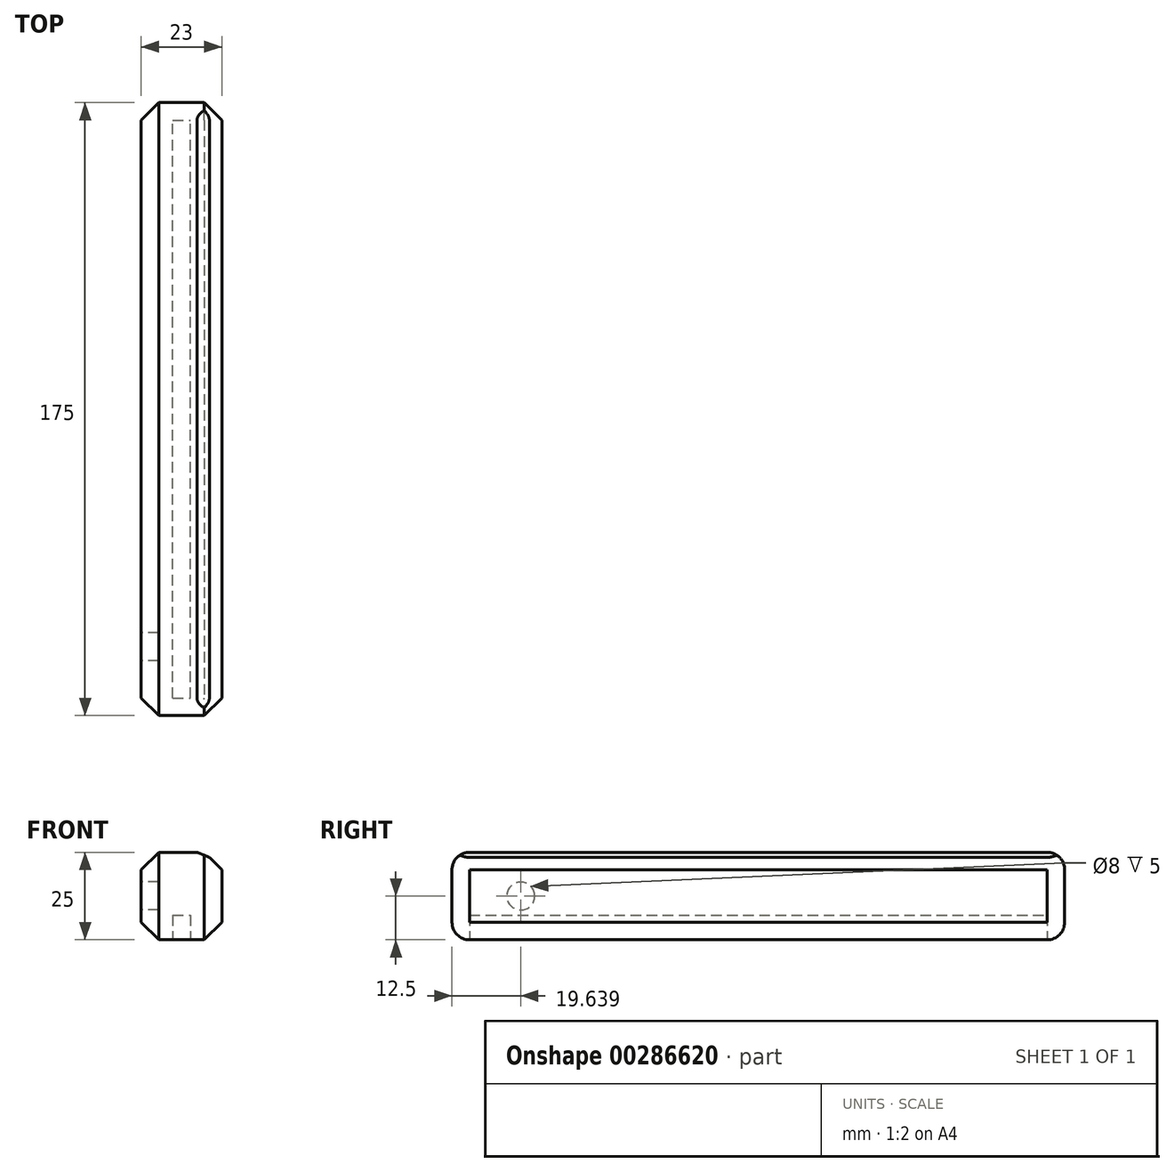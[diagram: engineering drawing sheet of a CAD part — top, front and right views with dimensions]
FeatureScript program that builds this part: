
annotation { "Feature Type Name" : "Feature", "Feature Type Description" : "" }
export const myFeature = defineFeature(function(context is Context, id is Id, definition is map)
    precondition{}
    {
        {
            var Q0;
            Q0=qCreatedBy(makeId("Front.planeOp"),FACE);
            var sketch = newSketch(context, id + "F0", { "sketchPlane" : qUnion([Q0])});
            skLineSegment(sketch, "E0.bottom", {"start": v(-11.5, 12.5) * mm, "end": v(11.5, 12.5) * mm});
            skLineSegment(sketch, "E0.top", {"start": v(-11.5, -12.5) * mm, "end": v(11.5, -12.5) * mm});
            skLineSegment(sketch, "E0.left", {"start": v(-11.5, 12.5) * mm, "end": v(-11.5, -12.5) * mm});
            skLineSegment(sketch, "E0.right", {"start": v(11.5, 12.5) * mm, "end": v(11.5, -12.5) * mm});
            skPoint(sketch, "E0.middle", {"position": v(0, 0) * mm});
            skSolve(sketch);
        }
        {
            var Q0;
            Q0=makeQuery(id+"F0.imprint","IMPRINT",FACE,{"disambiguationData":[TD([[makeQuery(id+"F0.imprint","IMPRINT",EDGE,{"derivedFrom":sQuery(id+"F0.wireOp",EDGE,"E0.bottom")}),-1.0]])]});
            extrude(context, id + "F1", {"entities" : qUnion([Q0]), "depth" : 175 * mm});
        }
        {
            var Q0;
            Q0=makeQuery(id+"F1.opExtrude","CAP_EDGE",EDGE,{"disambiguationData":[OSD([sQuery(id+"F0.wireOp",EDGE,"E0.bottom")])],"isStart":false});
            var Q1;
            Q1=makeQuery(id+"F1.opExtrude","CAP_EDGE",EDGE,{"disambiguationData":[OSD([sQuery(id+"F0.wireOp",EDGE,"E0.top")])],"isStart":false});
            var Q2;
            Q2=makeQuery(id+"F1.opExtrude","CAP_EDGE",EDGE,{"disambiguationData":[OSD([sQuery(id+"F0.wireOp",EDGE,"E0.bottom")])],"isStart":true});
            var Q3;
            Q3=makeQuery(id+"F1.opExtrude","CAP_EDGE",EDGE,{"disambiguationData":[OSD([sQuery(id+"F0.wireOp",EDGE,"E0.top")])],"isStart":true});
            fillet(context, id + "F2", {"entities" : qUnion([Q0, Q1, Q2, Q3]), "radius" : 5 * mm, "tangentPropagation" : true, "allowEdgeOverflow" : false});
        }
        {
            var Q0;
            Q0=makeQuery(id+"F1.opExtrude","SWEPT_FACE",FACE,{"disambiguationData":[OSD([sQuery(id+"F0.wireOp",EDGE,"E0.top")])]});
            var sketch = newSketch(context, id + "F3", { "sketchPlane" : qUnion([Q0])});
            skLineSegment(sketch, "E1.bottom", {"start": v(2.5, 170) * mm, "end": v(-2.5, 170) * mm});
            skLineSegment(sketch, "E1.top", {"start": v(2.5, 5) * mm, "end": v(-2.5, 5) * mm});
            skLineSegment(sketch, "E1.left", {"start": v(2.5, 170) * mm, "end": v(2.5, 5) * mm});
            skLineSegment(sketch, "E1.right", {"start": v(-2.5, 170) * mm, "end": v(-2.5, 5) * mm});
            skPoint(sketch, "E1.middle", {"position": v(0, 87.5) * mm});
            skPoint(sketch, "E1.middle.positionSnap0", {"position": v(11.5, 87.5) * mm});
            skPoint(sketch, "E1.centerSnap0", {"position": v(11.5, 87.5) * mm});
            skSolve(sketch);
        }
        {
            var Q0;
            Q0=makeQuery(id+"F3.imprint","IMPRINT",FACE,{"disambiguationData":[TD([[makeQuery(id+"F3.imprint","IMPRINT",EDGE,{"derivedFrom":sQuery(id+"F3.wireOp",EDGE,"E1.bottom")}),1.0]])]});
            extrude(context, id + "F4", {"entities" : qUnion([Q0]), "operationType" : NewBodyOperationType.REMOVE, "oppositeDirection" : true, "depth" : 7 * mm});
        }
        {
            var Q0;
            Q0=makeQuery(id+"F1.opExtrude","SWEPT_EDGE",EDGE,{"disambiguationData":[OSD([sQuery(id+"F0.wireOp",EDGE,"E0.bottom"),sQuery(id+"F0.wireOp",EDGE,"E0.right")])]});
            chamfer(context, id + "F5", {"entities" : qUnion([Q0]), "width" : 5 * mm, "tangentPropagation" : true});
        }
        {
            var Q0;
            Q0=makeQuery(id+"F1.opExtrude","SWEPT_FACE",FACE,{"disambiguationData":[OSD([sQuery(id+"F0.wireOp",EDGE,"E0.left")])]});
            var sketch = newSketch(context, id + "F6", { "sketchPlane" : qUnion([Q0])});
            skCircle(sketch, "E2", {"center": v(155.36, 0) * mm, "radius": 4 * mm});
            skSolve(sketch);
        }
        {
            var Q0;
            Q0=makeQuery(id+"F6.imprint","IMPRINT",FACE,{"disambiguationData":[TD([[makeQuery(id+"F6.imprint","IMPRINT",EDGE,{"derivedFrom":sQuery(id+"F6.wireOp",EDGE,"E2")}),1.0]])]});
            extrude(context, id + "F7", {"entities" : qUnion([Q0]), "operationType" : NewBodyOperationType.REMOVE, "oppositeDirection" : true, "depth" : 5 * mm});
        }
        {
            var Q0;
            Q0=makeQuery(id+"F1.opExtrude","SWEPT_FACE",FACE,{"disambiguationData":[OSD([sQuery(id+"F0.wireOp",EDGE,"E0.bottom")])]});
            chamfer(context, id + "F8", {"entities" : qUnion([Q0]), "width" : 5 * mm, "tangentPropagation" : true});
        }
    });
